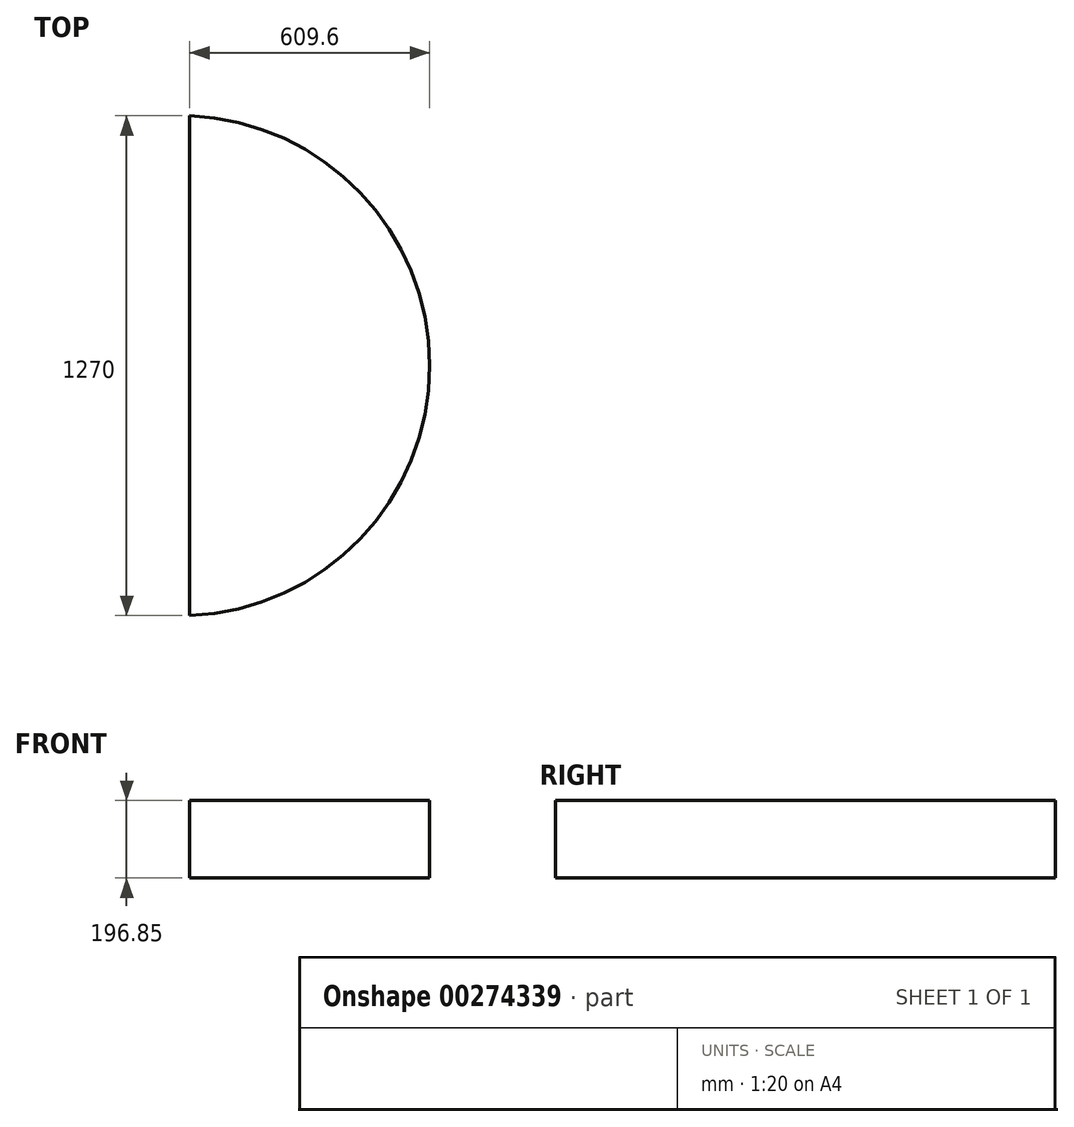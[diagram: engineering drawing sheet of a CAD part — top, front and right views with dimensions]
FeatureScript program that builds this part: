
annotation { "Feature Type Name" : "Feature", "Feature Type Description" : "" }
export const myFeature = defineFeature(function(context is Context, id is Id, definition is map)
    precondition{}
    {
        {
            var Q0;
            Q0=qCreatedBy(makeId("Top.planeOp"),FACE);
            var sketch = newSketch(context, id + "F0", { "sketchPlane" : qUnion([Q0])});
            skLineSegment(sketch, "E0", {"start": v(0, 0) * mm, "end": v(0, 514.76) * mm});
            skLineSegment(sketch, "E1", {"start": v(0, 514.76) * mm, "end": v(0, -755.24) * mm});
            skArc(sketch, "E2", {"start": v(0, -755.24) * mm, "mid": v(609.6, -120.24) * mm, "end": v(0, 514.76) * mm});
            skSolve(sketch);
        }
        {
            var Q0;
            Q0 = qSketchRegion(id + "F0", true);
            extrude(context, id + "F1", {"entities" : qUnion([Q0]), "depth" : 196.85 * mm});
        }
    });
